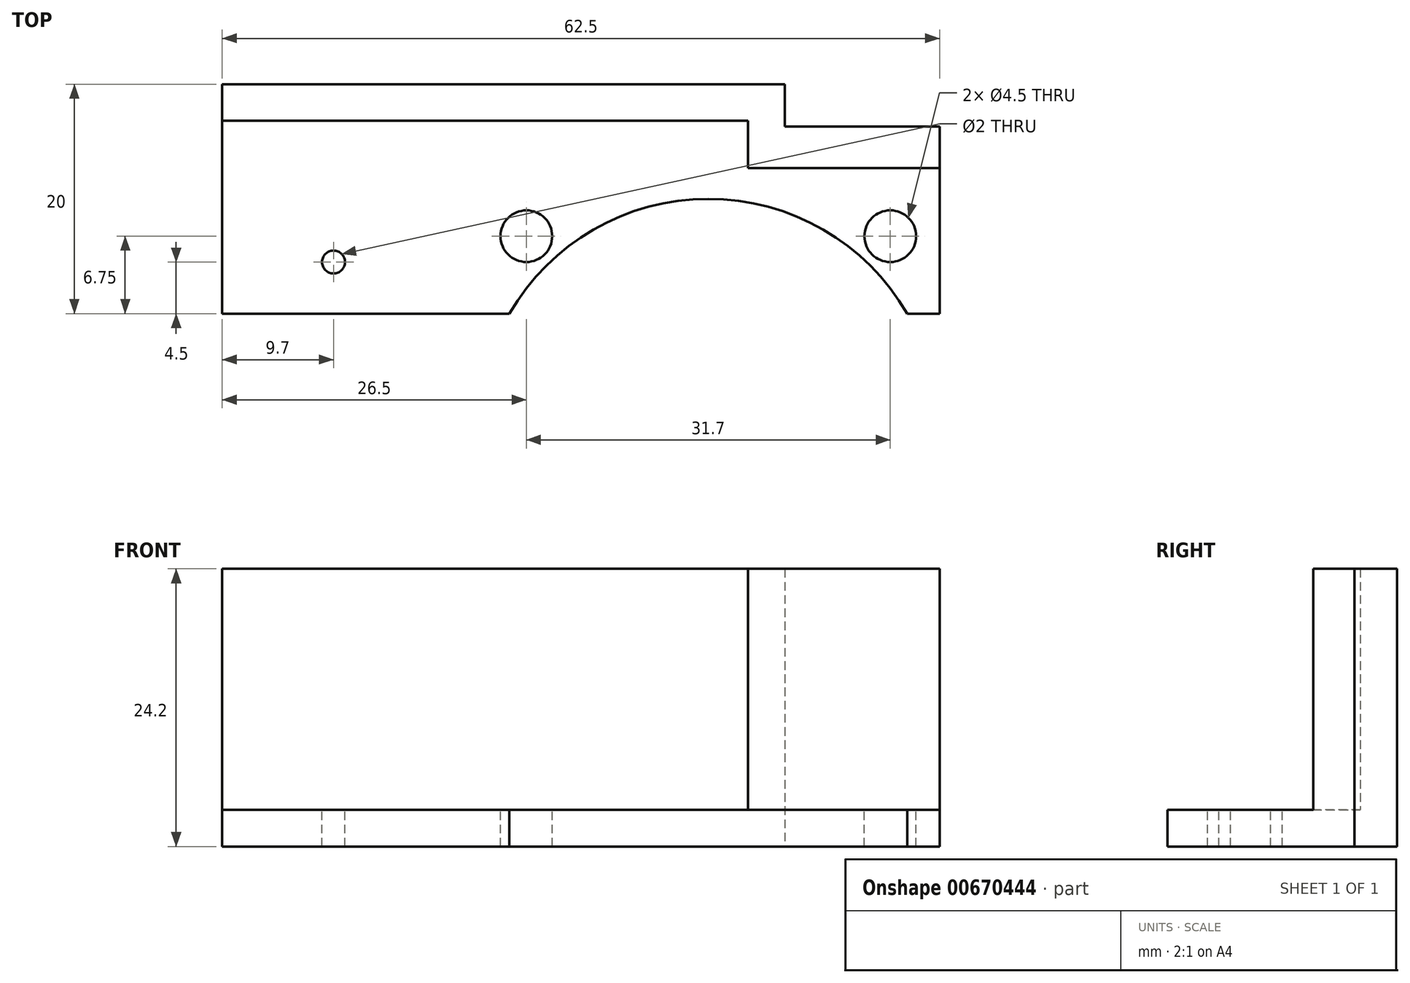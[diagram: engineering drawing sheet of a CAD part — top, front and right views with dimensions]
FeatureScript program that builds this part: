
annotation { "Feature Type Name" : "Feature", "Feature Type Description" : "" }
export const myFeature = defineFeature(function(context is Context, id is Id, definition is map)
    precondition{}
    {
        {
            var Q0;
            Q0=qCreatedBy(makeId("Top.planeOp"),FACE);
            var sketch = newSketch(context, id + "F0", { "sketchPlane" : qUnion([Q0])});
            skLineSegment(sketch, "E0", {"start": v(62.5, 0) * mm, "end": v(62.5, 16.3) * mm});
            skLineSegment(sketch, "E1", {"start": v(62.5, 16.3) * mm, "end": v(49, 16.3) * mm});
            skLineSegment(sketch, "E2", {"start": v(49, 16.3) * mm, "end": v(49, 20) * mm});
            skLineSegment(sketch, "E3", {"start": v(49, 20) * mm, "end": v(0, 20) * mm});
            skLineSegment(sketch, "E4", {"start": v(0, 20) * mm, "end": v(0, 0) * mm});
            skLineSegment(sketch, "E5", {"start": v(0, 20) * mm, "end": v(62.5, 20) * mm, "construction": true});
            skLineSegment(sketch, "E6", {"start": v(62.5, 20) * mm, "end": v(62.5, 0) * mm, "construction": true});
            skLineSegment(sketch, "E7", {"start": v(32.53, 20) * mm, "end": v(32.53, 10) * mm, "construction": true});
            skLineSegment(sketch, "E8", {"start": v(0, 0) * mm, "end": v(62.5, 0) * mm});
            skLineSegment(sketch, "E9", {"start": v(0, 10) * mm, "end": v(62.5, 10) * mm, "construction": true});
            skSolve(sketch);
        }
        {
            var Q0;
            Q0 = qSketchRegion(id + "F0", true);
            extrude(context, id + "F1", {"entities" : qUnion([Q0]), "depth" : 3.2 * mm, "offsetDistance" : 25 * mm});
        }
        {
            var Q0;
            Q0=makeQuery(id+"F1.opExtrude","CAP_FACE",FACE,{"disambiguationData":[OSD([sQuery(id+"F0.wireOp",EDGE,"E0"),sQuery(id+"F0.wireOp",EDGE,"E1"),sQuery(id+"F0.wireOp",EDGE,"E2"),sQuery(id+"F0.wireOp",EDGE,"E3"),sQuery(id+"F0.wireOp",EDGE,"E4"),sQuery(id+"F0.wireOp",EDGE,"E8")])],"isStart":false});
            var sketch = newSketch(context, id + "F2", { "sketchPlane" : qUnion([Q0])});
            skCircle(sketch, "E10", {"center": v(42.35, -10) * mm, "radius": 20 * mm});
            skLineSegment(sketch, "E11", {"start": v(0, 10) * mm, "end": v(62.5, 10) * mm, "construction": true});
            skLineSegment(sketch, "E12", {"start": v(0, -10) * mm, "end": v(42.35, -10) * mm, "construction": true});
            skLineSegment(sketch, "E13", {"start": v(34.54, 10) * mm, "end": v(34.54, -10) * mm, "construction": true});
            skLineSegment(sketch, "E14", {"start": v(0, 0) * mm, "end": v(25, 0) * mm, "construction": true});
            skSolve(sketch);
        }
        {
            var Q0;
            Q0 = qSketchRegion(id + "F2", true);
            extrude(context, id + "F3", {"entities" : qUnion([Q0]), "operationType" : NewBodyOperationType.REMOVE, "oppositeDirection" : true, "depth" : 25 * mm, "offsetDistance" : 25 * mm});
        }
        {
            var Q0;
            Q0=makeQuery(id+"F1.opExtrude","CAP_FACE",FACE,{"disambiguationData":[OSD([sQuery(id+"F0.wireOp",EDGE,"E0"),sQuery(id+"F0.wireOp",EDGE,"E1"),sQuery(id+"F0.wireOp",EDGE,"E2"),sQuery(id+"F0.wireOp",EDGE,"E3"),sQuery(id+"F0.wireOp",EDGE,"E4"),sQuery(id+"F0.wireOp",EDGE,"E8")])],"isStart":false});
            var sketch = newSketch(context, id + "F4", { "sketchPlane" : qUnion([Q0])});
            skCircle(sketch, "E15", {"center": v(9.7, 4.5) * mm, "radius": 1 * mm});
            skLineSegment(sketch, "E16", {"start": v(0, 4.5) * mm, "end": v(9.7, 4.5) * mm, "construction": true});
            skLineSegment(sketch, "E17", {"start": v(9.7, 4.5) * mm, "end": v(9.7, 20) * mm, "construction": true});
            skSolve(sketch);
        }
        {
            var Q0;
            Q0 = qSketchRegion(id + "F4", true);
            extrude(context, id + "F5", {"entities" : qUnion([Q0]), "operationType" : NewBodyOperationType.REMOVE, "oppositeDirection" : true, "depth" : 25 * mm, "offsetDistance" : 25 * mm});
        }
        {
            var Q0;
            Q0=makeQuery(id+"F1.opExtrude","CAP_FACE",FACE,{"disambiguationData":[OSD([sQuery(id+"F0.wireOp",EDGE,"E0"),sQuery(id+"F0.wireOp",EDGE,"E1"),sQuery(id+"F0.wireOp",EDGE,"E2"),sQuery(id+"F0.wireOp",EDGE,"E3"),sQuery(id+"F0.wireOp",EDGE,"E4"),sQuery(id+"F0.wireOp",EDGE,"E8")])],"isStart":false});
            var sketch = newSketch(context, id + "F6", { "sketchPlane" : qUnion([Q0])});
            skCircle(sketch, "E18", {"center": v(26.5, 6.75) * mm, "radius": 2.25 * mm});
            skCircle(sketch, "E19", {"center": v(58.2, 6.75) * mm, "radius": 2.25 * mm});
            skLineSegment(sketch, "E20", {"start": v(26.5, 20) * mm, "end": v(26.5, 6.75) * mm, "construction": true});
            skLineSegment(sketch, "E21", {"start": v(26.5, 6.75) * mm, "end": v(58.2, 6.75) * mm, "construction": true});
            skLineSegment(sketch, "E22", {"start": v(0, 6.74) * mm, "end": v(26.5, 6.74) * mm, "construction": true});
            skSolve(sketch);
        }
        {
            var Q0;
            Q0 = qSketchRegion(id + "F6", true);
            extrude(context, id + "F7", {"entities" : qUnion([Q0]), "operationType" : NewBodyOperationType.REMOVE, "oppositeDirection" : true, "depth" : 25 * mm, "offsetDistance" : 25 * mm});
        }
        {
            var Q0;
            Q0=makeQuery(id+"F1.opExtrude","CAP_FACE",FACE,{"disambiguationData":[OSD([sQuery(id+"F0.wireOp",EDGE,"E0"),sQuery(id+"F0.wireOp",EDGE,"E1"),sQuery(id+"F0.wireOp",EDGE,"E2"),sQuery(id+"F0.wireOp",EDGE,"E3"),sQuery(id+"F0.wireOp",EDGE,"E4"),sQuery(id+"F0.wireOp",EDGE,"E8")])],"isStart":false});
            var sketch = newSketch(context, id + "F8", { "sketchPlane" : qUnion([Q0])});
            skLineSegment(sketch, "E23", {"start": v(0, 20) * mm, "end": v(49, 20) * mm});
            skLineSegment(sketch, "E24", {"start": v(49, 20) * mm, "end": v(49, 16.3) * mm});
            skLineSegment(sketch, "E25", {"start": v(49, 16.3) * mm, "end": v(62.5, 16.3) * mm});
            skLineSegment(sketch, "E26", {"start": v(62.5, 16.3) * mm, "end": v(62.5, 12.7) * mm});
            skLineSegment(sketch, "E27", {"start": v(62.5, 12.7) * mm, "end": v(45.8, 12.7) * mm});
            skLineSegment(sketch, "E28", {"start": v(45.8, 12.7) * mm, "end": v(45.8, 16.8) * mm});
            skLineSegment(sketch, "E29", {"start": v(45.8, 16.8) * mm, "end": v(0, 16.8) * mm});
            skLineSegment(sketch, "E30", {"start": v(0, 16.8) * mm, "end": v(0, 20) * mm});
            skLineSegment(sketch, "E31", {"start": v(45.8, 16.8) * mm, "end": v(49, 16.8) * mm, "construction": true});
            skLineSegment(sketch, "E32", {"start": v(40.77, 16.8) * mm, "end": v(40.77, 20) * mm, "construction": true});
            skSolve(sketch);
        }
        {
            var Q0;
            Q0 = qSketchRegion(id + "F8", true);
            extrude(context, id + "F9", {"entities" : qUnion([Q0]), "operationType" : NewBodyOperationType.ADD, "depth" : 21 * mm, "offsetDistance" : 25 * mm});
        }
    });
